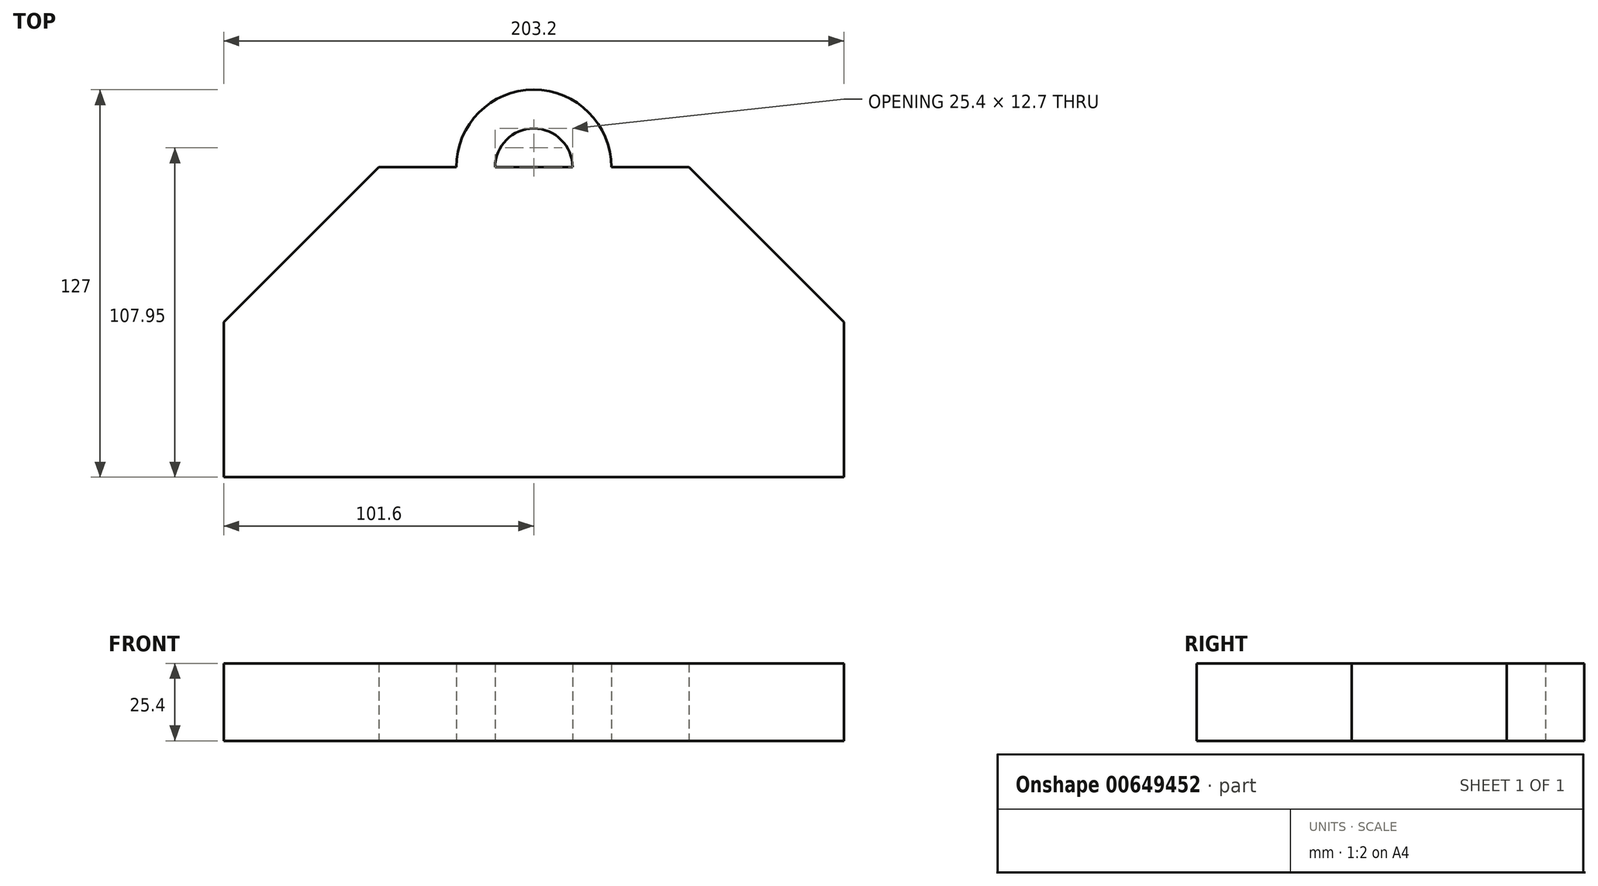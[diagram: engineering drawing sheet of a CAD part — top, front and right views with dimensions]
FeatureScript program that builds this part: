
annotation { "Feature Type Name" : "Feature", "Feature Type Description" : "" }
export const myFeature = defineFeature(function(context is Context, id is Id, definition is map)
    precondition{}
    {
        {
            var Q0;
            Q0=qCreatedBy(makeId("Top.planeOp"),FACE);
            var sketch = newSketch(context, id + "F0", { "sketchPlane" : qUnion([Q0])});
            skLineSegment(sketch, "E0", {"start": v(0, 0) * mm, "end": v(0, 50.8) * mm});
            skLineSegment(sketch, "E1", {"start": v(0, 50.8) * mm, "end": v(50.8, 101.6) * mm});
            skLineSegment(sketch, "E2", {"start": v(50.8, 101.6) * mm, "end": v(76.2, 101.6) * mm});
            skLineSegment(sketch, "E3", {"start": v(152.4, 101.6) * mm, "end": v(203.2, 50.8) * mm});
            skLineSegment(sketch, "E4", {"start": v(203.2, 50.8) * mm, "end": v(203.2, 0) * mm});
            skLineSegment(sketch, "E5", {"start": v(203.2, 0) * mm, "end": v(0, 0) * mm});
            skArc(sketch, "E6", {"start": v(127, 101.6) * mm, "mid": v(101.6, 127) * mm, "end": v(76.2, 101.6) * mm});
            skArc(sketch, "E7", {"start": v(114.3, 101.6) * mm, "mid": v(101.6, 114.3) * mm, "end": v(88.9, 101.6) * mm});
            skLineSegment(sketch, "E8.trimOffspring", {"start": v(88.9, 101.6) * mm, "end": v(114.3, 101.6) * mm});
            skLineSegment(sketch, "E9.trimOffspring", {"start": v(127, 101.6) * mm, "end": v(152.4, 101.6) * mm});
            skSolve(sketch);
        }
        {
            var Q0;
            Q0=makeQuery(id+"F0.imprint","IMPRINT",FACE,{"disambiguationData":[TD([[makeQuery(id+"F0.imprint","IMPRINT",EDGE,{"derivedFrom":sQuery(id+"F0.wireOp",EDGE,"E0")}),-1.0]])]});
            extrude(context, id + "F1", {"entities" : qUnion([Q0]), "depth" : 25.4 * mm, "offsetDistance" : 25.4 * mm});
        }
    });
